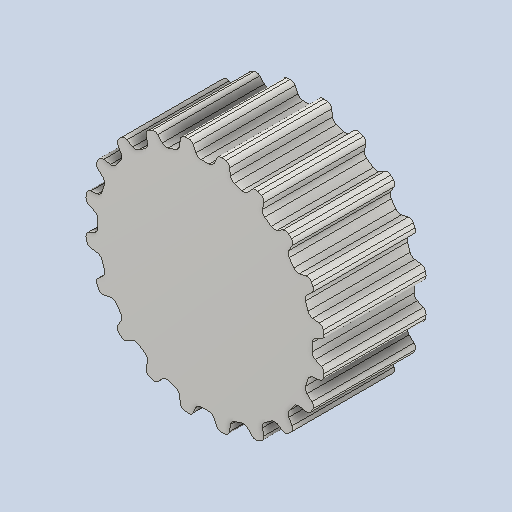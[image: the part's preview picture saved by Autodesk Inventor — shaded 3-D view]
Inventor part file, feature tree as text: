
AUTODESK INVENTOR PART (.ipt)
format: ipt  version: 2024 (Build 280153000, 153)  size: 289,280 bytes
history: native  units: mm (DEFAULTED — no unit token found)
features: other x3, extrude x2, fillet x1, pattern_circular x1
ambient origin geometry x8: Origin, YZ Plane, XZ Plane, XY Plane, X Axis, Y Axis, Z Axis, Center Point
bodies: Solid1 (feature_tree)
feature tree (7):
  other  "Pulley Sketch"
  extrude  "Base Body"  Depth=15.915494mm
  extrude  "Tooth"  Depth=0.3mm
  fillet  "Tooth Fillet"  Radius=0.8382mm
  pattern_circular  "Teeth"  [2 undecoded]
  other  "Left flange"
  other  "Right flange"
note: 2 required parameter values undecoded (feature->parameter linkage not recoverable at this tier; creation-order binding heuristic only, values carry confidence <= 0.55)
